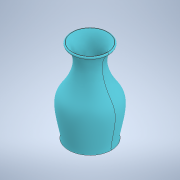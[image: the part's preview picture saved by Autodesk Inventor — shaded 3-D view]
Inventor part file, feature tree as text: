
AUTODESK INVENTOR PART (.ipt)
format: ipt  version: 2022 (Build 260153000, 153)  size: 348,160 bytes
history: native  units: mm
features: revolve x1, shell x1, fillet x1, sketch x1
ambient origin geometry x8: Origin, YZ Plane, XZ Plane, XY Plane, X Axis, Y Axis, Z Axis, Center Point
bodies: Solid1 (feature_tree)
feature tree (4):
  revolve  "Revolution1"  [1 undecoded]
  shell  "Shell1"  Thickness=90.0deg
  fillet  "Fillet1"  Radius=4.0mm
  sketch  "Sketch1"  dims[d0=4.0mm d1=15.0mm d2=90.0deg d3=4.0mm d4=90.0deg d5=0.4mm d6=0.2mm]
note: 1 required parameter value undecoded (feature->parameter linkage not recoverable at this tier; creation-order binding heuristic only, values carry confidence <= 0.55)
